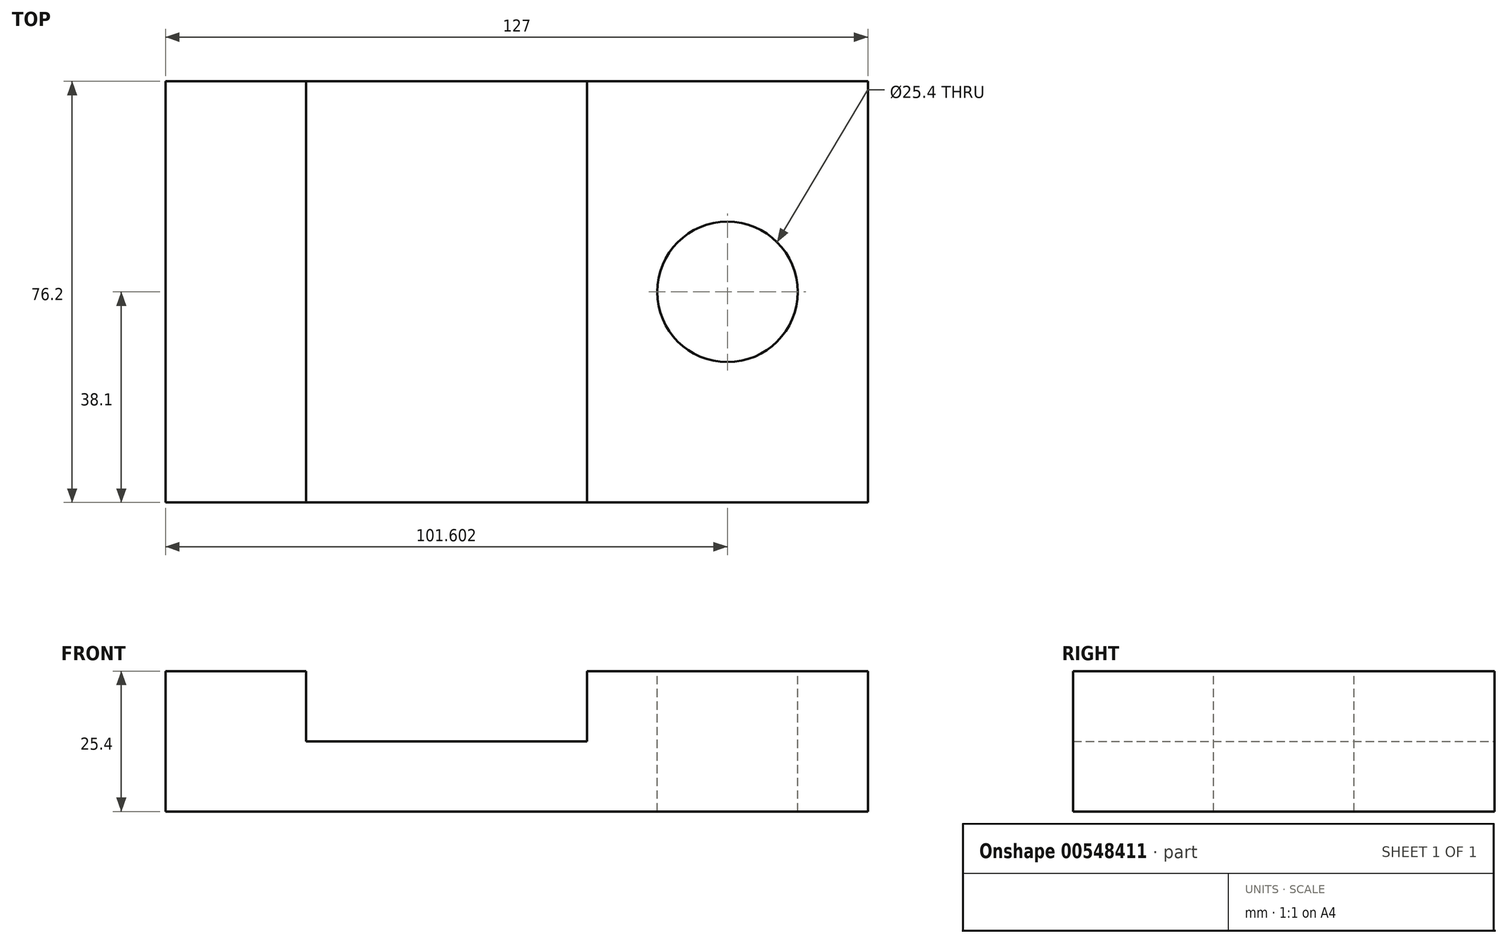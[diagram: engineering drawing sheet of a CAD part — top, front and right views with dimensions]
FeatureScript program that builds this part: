
annotation { "Feature Type Name" : "Feature", "Feature Type Description" : "" }
export const myFeature = defineFeature(function(context is Context, id is Id, definition is map)
    precondition{}
    {
        {
            var Q0;
            Q0=qCreatedBy(makeId("Front.planeOp"),FACE);
            var sketch = newSketch(context, id + "F0", { "sketchPlane" : qUnion([Q0])});
            skLineSegment(sketch, "E0", {"start": v(-64.28, 0) * mm, "end": v(-64.28, 25.4) * mm});
            skLineSegment(sketch, "E1", {"start": v(-64.28, 25.4) * mm, "end": v(-38.88, 25.4) * mm});
            skLineSegment(sketch, "E2", {"start": v(-38.88, 25.4) * mm, "end": v(-38.88, 12.7) * mm});
            skLineSegment(sketch, "E3", {"start": v(-38.88, 12.7) * mm, "end": v(11.92, 12.7) * mm});
            skLineSegment(sketch, "E4", {"start": v(11.92, 12.7) * mm, "end": v(11.92, 25.4) * mm});
            skLineSegment(sketch, "E5", {"start": v(-64.28, 0) * mm, "end": v(62.72, 0) * mm});
            skLineSegment(sketch, "E6", {"start": v(62.72, 0) * mm, "end": v(62.72, 25.4) * mm});
            skLineSegment(sketch, "E7", {"start": v(62.72, 25.4) * mm, "end": v(11.92, 25.4) * mm});
            skSolve(sketch);
        }
        {
            var Q0;
            Q0=makeQuery(id+"F0.imprint","IMPRINT",FACE,{"disambiguationData":[TD([[makeQuery(id+"F0.imprint","IMPRINT",EDGE,{"derivedFrom":sQuery(id+"F0.wireOp",EDGE,"E0")}),-1.0]])]});
            extrude(context, id + "F1", {"entities" : qUnion([Q0]), "depth" : 76.2 * mm, "offsetDistance" : 25.4 * mm, "symmetric" : true});
        }
        {
            var Q0;
            Q0=makeQuery(id+"F1.opExtrude","SWEPT_FACE",FACE,{"disambiguationData":[OSD([sQuery(id+"F0.wireOp",EDGE,"E7")])]});
            var sketch = newSketch(context, id + "F2", { "sketchPlane" : qUnion([Q0])});
            skCircle(sketch, "E8", {"center": v(37.32, 0) * mm, "radius": 12.7 * mm});
            skSolve(sketch);
        }
        {
            var Q0;
            Q0=sQuery(id+"F2.wireOp",VERTEX,"E8.center");
            var Q1;
            Q1=makeQuery(id+"F1.opExtrude","SWEPT_BODY",BODY,{"disambiguationData":[OSD([sQuery(id+"F0.wireOp",EDGE,"E0"),sQuery(id+"F0.wireOp",EDGE,"E1"),sQuery(id+"F0.wireOp",EDGE,"E2"),sQuery(id+"F0.wireOp",EDGE,"E3"),sQuery(id+"F0.wireOp",EDGE,"E4"),sQuery(id+"F0.wireOp",EDGE,"E5"),sQuery(id+"F0.wireOp",EDGE,"E6"),sQuery(id+"F0.wireOp",EDGE,"E7")])]});
            hole(context, id + "F3", {"style" : HoleStyle.SIMPLE, "endStyle" : HoleEndStyle.THROUGH, "holeDiameter" : 25.4 * mm, "isTappedThrough" : true, "tappedDepth" : 12.7 * mm, "tapClearance" : 3, "locations" : qUnion([Q0]), "scope" : qUnion([Q1])});
        }
    });
